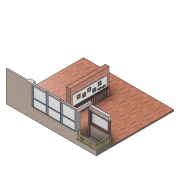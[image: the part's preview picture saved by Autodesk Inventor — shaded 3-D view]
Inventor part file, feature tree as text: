
AUTODESK INVENTOR PART (.ipt)
format: ipt  version: 2020.2 (Build 242310000, 310)  size: 1,736,192 bytes
history: native  units: mm
features: extrude x49, plane x45, sketch x36, other x4, loft x4, fillet x2, emboss x1
ambient origin geometry x8: Origin, YZ Plane, XZ Plane, XY Plane, X Axis, Y Axis, Z Axis, Center Point
bodies: Solid1 (feature_tree), Solid2 (feature_tree), Solid3 (feature_tree), Solid4 (feature_tree), Solid5 (feature_tree), Solid6 (feature_tree), Solid7 (feature_tree)
feature tree (141):
  extrude  "Extrusion1"  Depth=6000.0mm
  other  "Pod plane"
  other  "D. deo, terasa i prozori"
  plane  "Work Plane2"
  extrude  "Extrusion2"  TaperAngle=0.0deg  [1 undecoded]
  plane  "Work Plane3"
  sketch  "Sketch10"  dims[d22=100.0mm d23=100.0mm]
  extrude  "Extrusion3"  Depth=100.0mm
  extrude  "Extrusion4"  Depth=1000.0mm
  extrude  "Extrusion6"  Depth=1000.0mm
  extrude  "Extrusion7"  Depth=300.0mm
  extrude  "Extrusion8"  Depth=2000.0mm TaperAngle=0.0deg
  plane  "Work Plane4"
  plane  "Work Plane5"
  extrude  "Extrusion10"  Depth=150.0mm
  fillet  "Fillet1"  Radius=100.0mm
  plane  "Work Plane7"
  plane  "Work Plane8"
  extrude  "Extrusion11"  Depth=30.0mm
  plane  "Work Plane9"
  sketch  "Sketch15"  dims[d32=0.0mm d33=300.0mm]
  extrude  "Extrusion12"  Depth=10.0mm TaperAngle=0.0deg
  extrude  "Extrusion13"  Depth=50.0mm
  extrude  "Extrusion14"  Depth=50.0mm
  extrude  "Extrusion15"  Depth=25.0mm
  plane  "Work Plane10"
  plane  "Work Plane11"
  plane  "Work Plane12"
  sketch  "Sketch19"  dims[d93=40.0mm d94=30.0mm]
  extrude  "Extrusion18"  Depth=20.0mm TaperAngle=0.0deg
  extrude  "Extrusion19"  Depth=250.0mm TaperAngle=0.0deg
  plane  "Work Plane13"
  extrude  "Extrusion20"  TaperAngle=0.0deg  [1 undecoded]
  plane  "Work Plane14"
  extrude  "Extrusion21"  Depth=10.0mm
  plane  "Work Plane15"
  plane  "Work Plane16"
  extrude  "Extrusion22"  Depth=10.0mm
  plane  "Work Plane17"
  extrude  "Extrusion23"  Depth=200.0mm TaperAngle=0.0deg
  extrude  "Extrusion24"  TaperAngle=0.0deg  [1 undecoded]
  plane  "Work Plane18"
  plane  "Work Plane19"
  sketch  "Sketch28"  dims[d133=2.0mm d134=0.0mm d135=50.0mm]
  plane  "Work Plane20"
  extrude  "Extrusion25"  Depth=10.0mm
  extrude  "Extrusion26"  Depth=500.0mm TaperAngle=0.0deg
  plane  "Work Plane21"
  extrude  "Extrusion27"  Depth=250.0mm
  extrude  "Extrusion29"  Depth=250.0mm
  loft  "Loft1"
  loft  "Loft2"
  extrude  "Extrusion30"  Depth=5.0mm TaperAngle=0.0deg
  plane  "Work Plane22"
  plane  "Work Plane23"
  extrude  "Extrusion31"  TaperAngle=0.0deg  [1 undecoded]
  extrude  "Extrusion32"  Depth=20.0mm
  plane  "Work Plane24"
  loft  "Loft3"
  loft  "Loft4"
  extrude  "Extrusion33"  Depth=750.0mm TaperAngle=0.0deg
  extrude  "Extrusion34"  Depth=750.0mm
  plane  "Work Plane25"
  plane  "Work Plane26"
  plane  "Work Plane27"
  extrude  "Extrusion35"  Depth=30.0mm
  extrude  "Extrusion36"  Depth=15.0mm
  plane  "Work Plane28"
  extrude  "Extrusion37"  Depth=1000.0mm
  plane  "Work Plane29"
  extrude  "Extrusion38"  Depth=1550.0mm TaperAngle=0.0deg
  plane  "Work Plane30"
  extrude  "Extrusion39"  TaperAngle=0.0deg  [1 undecoded]
  plane  "Work Plane31"
  plane  "Work Plane32"
  plane  "Work Plane33"
  extrude  "Extrusion42"  Depth=42.5mm
  plane  "Work Plane34"
  sketch  "Sketch59"  dims[d182=250.0mm d187=250.0mm d188=250.0mm]
  plane  "Work Plane36"
  sketch  "Sketch60"  dims[d189=250.0mm d190=250.0mm d191=250.0mm d192=250.0mm]
  plane  "Work Plane37"
  extrude  "Extrusion43"  Depth=42.5mm
  extrude  "Extrusion44"  Depth=1500.0mm
  extrude  "Extrusion45"  Depth=132.5mm TaperAngle=0.0deg
  extrude  "Extrusion46"  TaperAngle=0.0deg  [1 undecoded]
  plane  "Work Plane38"
  extrude  "Extrusion47"  TaperAngle=0.0deg  [1 undecoded]
  plane  "Work Plane39"
  extrude  "Extrusion48"  Depth=20.0mm TaperAngle=0.0deg
  plane  "Work Plane40"
  extrude  "Extrusion49"  TaperAngle=0.0deg  [1 undecoded]
  plane  "Work Plane41"
  extrude  "Extrusion50"  Depth=600.0mm TaperAngle=0.0deg
  plane  "Work Plane42"
  extrude  "Extrusion51"  Depth=400.0mm
  plane  "Work Plane43"
  plane  "Work Plane47"
  extrude  "Extrusion55"  Depth=2250.0mm TaperAngle=0.0deg
  plane  "Work Plane48"
  extrude  "Extrusion56"  TaperAngle=0.0deg  [1 undecoded]
  plane  "Work Plane49"
  plane  "Work Plane50"
  extrude  "Extrusion57"  Depth=700.0mm
  plane  "Work Plane51"
  emboss  "Emboss1"
  sketch  "Sketch1"  dims[d0=7000.0mm d1=6000.0mm]
  sketch  "Sketch9"  dims[d2=100.0mm d3=0.0mm d7=0.0mm]
  sketch  "Sketch12"  dims[d24=1400.0mm d25=1000.0mm]
  sketch  "Sketch14"  dims[d26=1500.0mm d27=1000.0mm]
  sketch  "Sketch20"  dims[d129=150.0mm d131=10.0mm d132=0.0mm]
  sketch  "Sketch29"  dims[d136=50.0mm d137=50.0mm]
  sketch  "Sketch38"  dims[d138=25.0mm d141=25.0mm]
  sketch  "Sketch39"  dims[d142=250.0mm d143=0.0mm d144=20.0mm d145=0.0mm]
  sketch  "Sketch40"  dims[d146=30.0mm d147=250.0mm d148=0.0mm]
  sketch  "Sketch42"  dims[d149=0.0mm d162=0.0mm]
  sketch  "Sketch44"  dims[d163=10.0mm d164=10.0mm]
  other  "Edges2"
  other  "Edges1"
  sketch  "Sketch50"  dims[d165=120.0mm d166=10.0mm]
  sketch  "Sketch52"  dims[d167=10.0mm d168=200.0mm d169=0.0mm]
  sketch  "Sketch53"  dims[d170=20.0mm d172=0.0mm]
  sketch  "Sketch54"  dims[d173=0.0mm d174=10.0mm]
  sketch  "Sketch55"  dims[d177=10.0mm d178=500.0mm d179=0.0mm]
  sketch  "Sketch58"  dims[d180=0.0mm d181=250.0mm]
  sketch  "Sketch61"  dims[d193=250.0mm d194=250.0mm d195=15.0mm d196=0.0mm]
  sketch  "Sketch64"  dims[d197=5.0mm d198=0.0mm d199=5.0mm d200=0.0mm]
  sketch  "Sketch65"  dims[d201=15.0mm d202=0.0mm d203=0.0mm]
  sketch  "Sketch66"  dims[d204=30.0mm d205=25.0mm d206=25.0mm d207=50.0mm d208=50.0mm d209=50.0mm d210=150.0mm d211=30.0mm d212=40.0mm d213=100.0mm d214=150.0mm d216=0.0mm d217=20.0mm d218=0.0mm]
  sketch  "Sketch67"  dims[d219=10.0mm d220=10.0mm d221=10.0mm d222=120.0mm d223=10.0mm d225=0.0mm d226=200.0mm d227=20.0mm]
  sketch  "Sketch68"  dims[d228=0.0mm d229=150.0mm]
  sketch  "Sketch69"  dims[d230=100.0mm d231=200.0mm]
  sketch  "Sketch75"  dims[d232=750.0mm d233=0.0mm d234=750.0mm d235=0.0mm]
  sketch  "Sketch76"  dims[d236=0.0mm d237=750.0mm]
  sketch  "Sketch78"  dims[d238=75.0mm d239=30.0mm]
  sketch  "Sketch80"  dims[d240=30.0mm d241=15.0mm d242=1000.0mm d243=1550.0mm d244=0.0mm d245=0.0mm d247=42.5mm d248=42.5mm d249=1500.0mm d250=132.5mm d251=0.0mm d252=0.0mm d257=0.0mm d258=20.0mm d259=20.0mm d260=0.0mm d261=0.0mm d262=0.0mm d265=600.0mm d266=0.0mm d267=400.0mm d270=2250.0mm d271=0.0mm d272=0.0mm d278=700.0mm d280=100.0mm d281=100.0mm d282=1000.0mm d283=100.0mm d284=100.0mm d285=1000.0mm d286=1000.0mm d287=0.0mm d288=40.0mm d289=1400.0mm d290=0.0mm d291=20.0mm d292=20.0mm d293=1450.0mm d294=0.0mm d295=0.0mm d296=42.5mm d297=42.5mm d299=22.5mm d300=55.0mm d301=1500.0mm d302=0.0mm d305=1650.0mm d306=0.0mm d309=50.0mm d310=50.0mm d311=30.0mm d312=30.0mm d313=0.0mm d314=90.0deg d315=0.0mm d316=90.0deg d317=30.0mm d319=30.0mm d320=50.0mm d321=200.0mm d322=70.0mm d323=0.0mm d324=90.0deg d325=0.0mm d326=90.0deg d327=1500.0mm d328=0.0mm d329=0.0mm d330=0.0mm d331=150.0mm d332=10.0mm d333=0.0mm d334=150.0mm d335=10.0mm d336=0.0mm d337=950.0mm d338=0.0mm d339=90.0deg d340=0.0mm d341=90.0deg d342=0.0mm d343=90.0deg d344=0.0mm d345=90.0deg d346=30.0mm d347=30.0mm d348=0.0mm d349=0.0mm d350=70.0mm d351=70.0mm d352=250.0mm d353=0.0mm d354=250.0mm d362=750.0mm d374=0.0mm d375=95.0mm d376=120.0mm d377=3478.0mm d378=0.0mm d379=40.0mm d380=1500.0mm d381=0.0mm d382=0.0mm d383=843.0mm d384=0.0mm d385=0.0mm d386=50.0mm d387=0.0mm d388=60.0mm d389=0.0mm d390=1500.0mm d391=0.0mm d392=0.0mm d396=0.0mm d399=0.0mm d400=29.375mm d401=29.375mm d402=1500.0mm d403=40.0mm d404=0.0mm d405=0.0mm d407=75.0mm d425=20.0mm d427=0.0mm d428=75.0mm d429=100.0mm d430=0.0mm d431=75.0mm d432=100.0mm d433=1000.0mm d434=0.0mm d435=1500.0mm d436=0.0mm d437=20.0mm d438=20.0mm d439=20.0mm d440=20.0mm d441=20.0mm d442=20.0mm d443=20.0mm d444=20.0mm d445=20.0mm d446=20.0mm d448=20.0mm d461=350.0mm d462=0.0mm d463=60.0mm d464=60.0mm d465=1370.0mm d466=0.0mm d468=0.0mm d469=30.0mm d473=200.0mm d474=0.0mm d475=0.0mm d476=85.0mm d477=1518.0mm d478=60.0mm d479=0.0mm d480=0.0mm d481=0.0mm d482=300.0mm d483=0.0mm d484=0.0mm d485=95.0mm d486=1600.0mm d487=0.0mm d488=0.0mm d489=6.0mm d490=3250.0mm d491=0.0mm d492=0.0mm d506=0.0mm d507=100.0mm d508=120.0mm d509=3450.0mm d510=0.0mm d511=0.0mm d512=1.0mm d513=0.0mm d514=0.0mm d515=0.0mm d516=20.0mm d517=0.0mm d518=0.0mm d519=10.0mm d520=0.0mm d307=0.5mm d308=0.872665mm]
  sketch  "Sketch17"  dims[d37=0.0mm d41=150.0mm d91=100.0mm]
  fillet  "Fillet2"  Radius=100.0mm
  extrude  "Extrusion16"  Depth=100.0mm
  extrude  "Extrusion17"  Depth=1000.0mm
  sketch  "Sketch16"  dims[d34=3000.0mm d35=2000.0mm d36=0.0mm]
note: 9 required parameter values undecoded (feature->parameter linkage not recoverable at this tier; creation-order binding heuristic only, values carry confidence <= 0.55)
